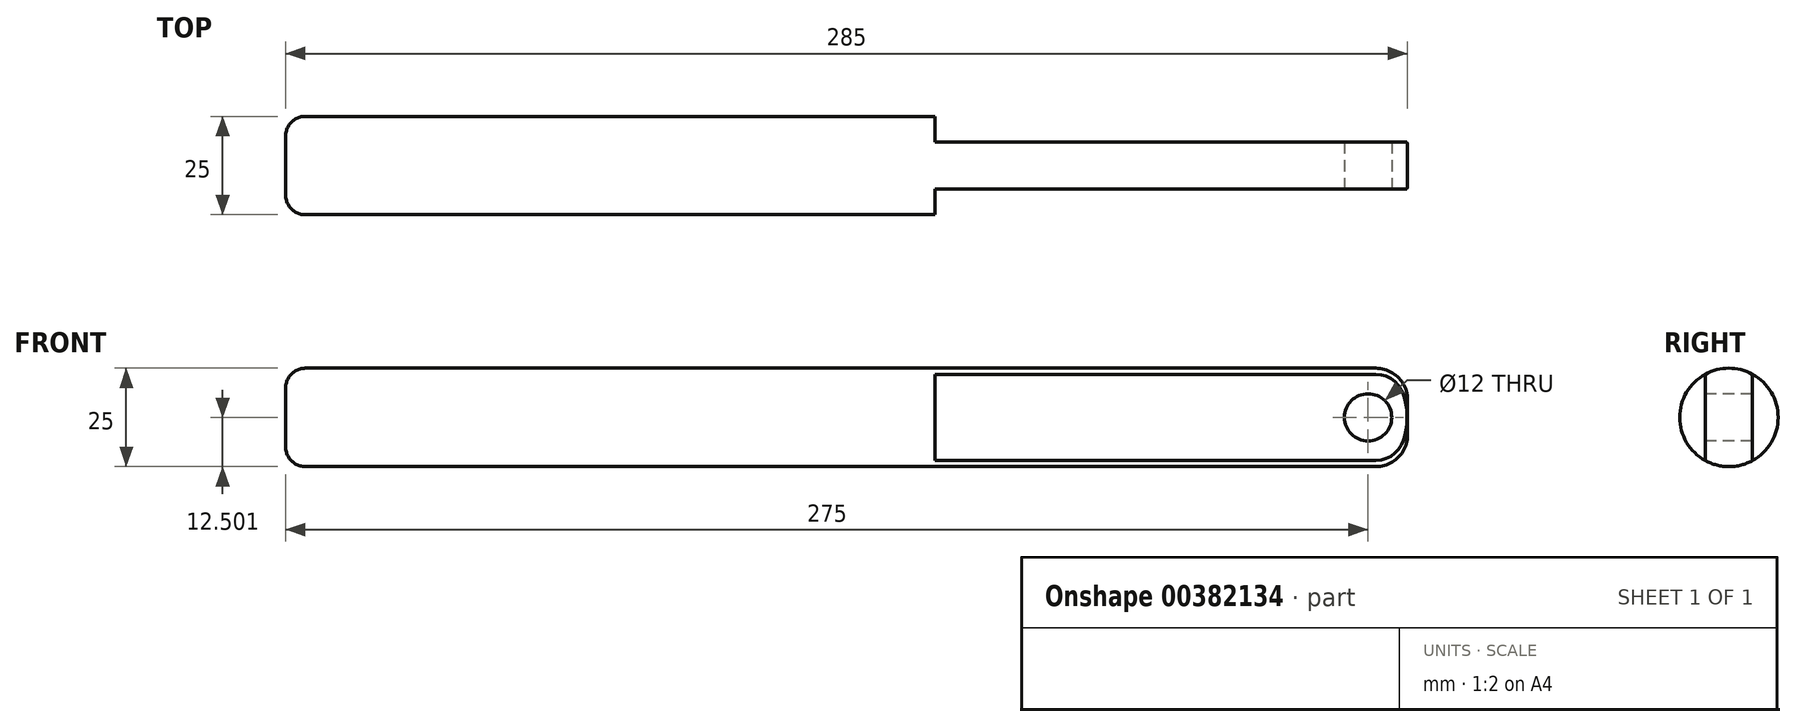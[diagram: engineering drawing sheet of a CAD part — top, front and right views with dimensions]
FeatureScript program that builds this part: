
annotation { "Feature Type Name" : "Feature", "Feature Type Description" : "" }
export const myFeature = defineFeature(function(context is Context, id is Id, definition is map)
    precondition{}
    {
        {
            var Q0;
            Q0=qCreatedBy(makeId("Right.planeOp"),FACE);
            var sketch = newSketch(context, id + "F0", { "sketchPlane" : qUnion([Q0])});
            skCircle(sketch, "E0", {"center": v(0, 79.47) * mm, "radius": 12.5 * mm});
            skSolve(sketch);
        }
        {
            var Q0;
            Q0=makeQuery(id+"F0.imprint","IMPRINT",FACE,{"disambiguationData":[TD([[makeQuery(id+"F0.imprint","IMPRINT",EDGE,{"derivedFrom":sQuery(id+"F0.wireOp",EDGE,"E0")}),1.0]])]});
            extrude(context, id + "F1", {"entities" : qUnion([Q0]), "oppositeDirection" : true, "depth" : 165 * mm});
        }
        {
            var Q0;
            Q0=makeQuery(id+"F1.opExtrude","CAP_EDGE",EDGE,{"disambiguationData":[OSD([sQuery(id+"F0.wireOp",EDGE,"E0")])],"isStart":false});
            fillet(context, id + "F2", {"entities" : qUnion([Q0]), "radius" : 5 * mm, "tangentPropagation" : true, "allowEdgeOverflow" : false});
        }
        {
            var Q0;
            Q0=makeQuery(id+"F1.opExtrude","CAP_FACE",FACE,{"disambiguationData":[OSD([sQuery(id+"F0.wireOp",EDGE,"E0")])],"isStart":true});
            var sketch = newSketch(context, id + "F3", { "sketchPlane" : qUnion([Q0])});
            skSolve(sketch);
        }
        {
            var Q0;
            Q0=makeQuery(id+"F3.imprint","IMPRINT",FACE,{"disambiguationData":[TD([[makeQuery(id+"F3.imprint","IMPRINT",EDGE,{"derivedFrom":makeQuery(id+"F1.opExtrude","CAP_EDGE",EDGE,{"disambiguationData":[OSD([sQuery(id+"F0.wireOp",EDGE,"E0")])],"isStart":true})}),1.0]])]});
            var sketch = newSketch(context, id + "F4", { "sketchPlane" : qUnion([Q0])});
            skLineSegment(sketch, "E1.left", {"start": v(-6, 90.44) * mm, "end": v(-6, 68.5) * mm});
            skLineSegment(sketch, "E1.right", {"start": v(6, 90.44) * mm, "end": v(6, 68.5) * mm});
            skArc(sketch, "E2", {"start": v(6, 90.44) * mm, "mid": v(0, 91.97) * mm, "end": v(-6, 90.44) * mm});
            skArc(sketch, "E3", {"start": v(-6, 68.5) * mm, "mid": v(0, 66.97) * mm, "end": v(6, 68.5) * mm});
            skSolve(sketch);
        }
        {
            var Q0;
            Q0 = qSketchRegion(id + "F4", true);
            extrude(context, id + "F5", {"entities" : qUnion([Q0]), "operationType" : NewBodyOperationType.ADD, "depth" : 120 * mm});
        }
        {
            var Q0;
            Q0=makeQuery(id+"F5.opExtrude","SWEPT_FACE",FACE,{"disambiguationData":[OSD([sQuery(id+"F4.wireOp",EDGE,"E1.left")])]});
            var sketch = newSketch(context, id + "F6", { "sketchPlane" : qUnion([Q0])});
            skCircle(sketch, "E4", {"center": v(110, 79.47) * mm, "radius": 6 * mm});
            skPoint(sketch, "E4.centerSnap0", {"position": v(120, 79.47) * mm});
            skSolve(sketch);
        }
        {
            var Q0;
            Q0=makeQuery(id+"F6.imprint","IMPRINT",FACE,{"disambiguationData":[TD([[makeQuery(id+"F6.imprint","IMPRINT",EDGE,{"derivedFrom":sQuery(id+"F6.wireOp",EDGE,"E4")}),1.0]])]});
            extrude(context, id + "F7", {"entities" : qUnion([Q0]), "operationType" : NewBodyOperationType.REMOVE, "endBound" : BoundingType.THROUGH_ALL, "oppositeDirection" : true, "depth" : 25 * mm});
        }
        {
            var Q0;
            Q0=makeQuery(id+"F5.opExtrude","CAP_EDGE",EDGE,{"disambiguationData":[OSD([sQuery(id+"F4.wireOp",EDGE,"E3")])],"isStart":false});
            fillet(context, id + "F8", {"entities" : qUnion([Q0]), "radius" : 8 * mm, "tangentPropagation" : true, "allowEdgeOverflow" : false});
        }
    });
